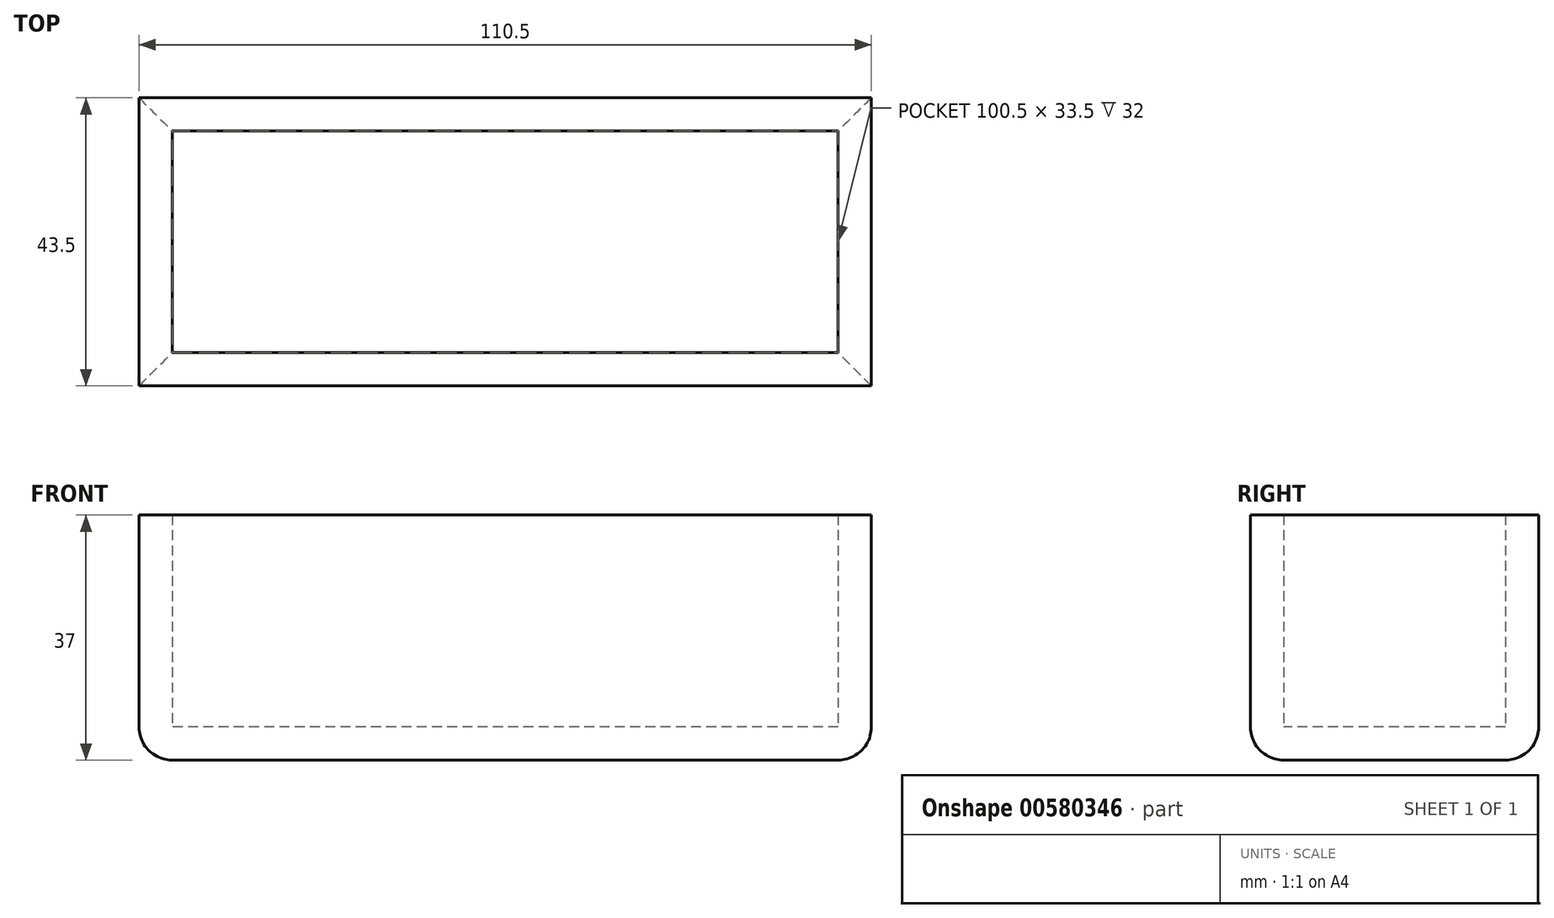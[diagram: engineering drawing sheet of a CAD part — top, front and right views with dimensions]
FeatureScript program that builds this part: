
annotation { "Feature Type Name" : "Feature", "Feature Type Description" : "" }
export const myFeature = defineFeature(function(context is Context, id is Id, definition is map)
    precondition{}
    {
        {
            var Q0;
            Q0=qCreatedBy(makeId("Top.planeOp"),FACE);
            var sketch = newSketch(context, id + "F0", { "sketchPlane" : qUnion([Q0])});
            skLineSegment(sketch, "E0.bottom", {"start": v(55.25, 21.75) * mm, "end": v(-55.25, 21.75) * mm});
            skLineSegment(sketch, "E0.top", {"start": v(55.25, -21.75) * mm, "end": v(-55.25, -21.75) * mm});
            skLineSegment(sketch, "E0.left", {"start": v(55.25, 21.75) * mm, "end": v(55.25, -21.75) * mm});
            skLineSegment(sketch, "E0.right", {"start": v(-55.25, 21.75) * mm, "end": v(-55.25, -21.75) * mm});
            skPoint(sketch, "E0.middle", {"position": v(0, 0) * mm});
            skLineSegment(sketch, "E1.bottom", {"start": v(50.25, 16.75) * mm, "end": v(-50.25, 16.75) * mm});
            skLineSegment(sketch, "E1.top", {"start": v(50.25, -16.75) * mm, "end": v(-50.25, -16.75) * mm});
            skLineSegment(sketch, "E1.left", {"start": v(50.25, 16.75) * mm, "end": v(50.25, -16.75) * mm});
            skLineSegment(sketch, "E1.right", {"start": v(-50.25, 16.75) * mm, "end": v(-50.25, -16.75) * mm});
            skSolve(sketch);
        }
        {
            var Q0;
            Q0=makeQuery(id+"F0.imprint","IMPRINT",FACE,{"disambiguationData":[TD([[makeQuery(id+"F0.imprint","IMPRINT",EDGE,{"derivedFrom":sQuery(id+"F0.wireOp",EDGE,"E1.bottom")}),1.0]])]});
            extrude(context, id + "F1", {"entities" : qUnion([Q0]), "depth" : 5 * mm, "offsetDistance" : 25 * mm});
        }
        {
            var Q0;
            Q0=makeQuery(id+"F0.imprint","IMPRINT",FACE,{"disambiguationData":[TD([[makeQuery(id+"F0.imprint","IMPRINT",EDGE,{"derivedFrom":sQuery(id+"F0.wireOp",EDGE,"E0.bottom")}),1.0]])]});
            extrude(context, id + "F2", {"entities" : qUnion([Q0]), "operationType" : NewBodyOperationType.ADD, "depth" : 37 * mm, "offsetDistance" : 25 * mm});
        }
        {
            var Q0;
            Q0=makeQuery(id+"F2.opExtrude","CAP_EDGE",EDGE,{"disambiguationData":[OSD([sQuery(id+"F0.wireOp",EDGE,"E0.right")])],"isStart":true});
            var Q1;
            Q1=makeQuery(id+"F2.opExtrude","CAP_EDGE",EDGE,{"disambiguationData":[OSD([sQuery(id+"F0.wireOp",EDGE,"E0.bottom")])],"isStart":true});
            var Q2;
            Q2=makeQuery(id+"F2.opExtrude","CAP_EDGE",EDGE,{"disambiguationData":[OSD([sQuery(id+"F0.wireOp",EDGE,"E0.left")])],"isStart":true});
            var Q3;
            Q3=makeQuery(id+"F2.opExtrude","CAP_EDGE",EDGE,{"disambiguationData":[OSD([sQuery(id+"F0.wireOp",EDGE,"E0.top")])],"isStart":true});
            fillet(context, id + "F3", {"entities" : qUnion([Q0, Q1, Q2, Q3]), "radius" : 5 * mm, "tangentPropagation" : true, "allowEdgeOverflow" : false});
        }
    });
